# Revit family: BIG-1150-N
name_source: partatom
category: Plumbing Fixtures
units: mm (PartAtom-declared; Revit-internal decimal feet)

## family parameters
Always vertical = Yes
Cut with Voids When Loaded = Yes
OmniClass Number = 23.45.00.00
OmniClass Title = Sanitary, Laundry, and Cleaning Equipment
Part Type = Normal
Room Calculation Point = No
Round Connector Dimension = Use Diameter
Shared = No
Work Plane-Based = No

## types (1)
- BIG-1150-N
    Bottom Pipe RP = 8 13/32"
    Default Elevation = 0"
    Ext End = -20"
    Front Extude = 27 1/2"
    Height of Body = 50"
    Length = 83"
    Lid Height from Inlet/Outlet Center (15.5" Min. thru 24.5" Max.) = 24 1/4"
    Manufacturer = MIFAB
    Material = Polyethylene, High Density
    Model = BIG-1150-N
    Pipe RP = 38"
    Top RP 1 = 19"
    Top Vent = 9 7/16"
    URL = WWW,MIFAB.COM
    Vent = 40"
    Vent Pipe = 0"
    Vent height = 40"
    Vent/2 = 20"
    Vesibility-Vent = Yes
    Visibility-1 = No
    Visiblity = Yes
    Void 1 H = 6 1/16"
    Void 1 L = 14 9/32"
    Void 1 TL = 9 15/32"
    Width = 33 1/2"
    array = 2
    center void = 10"
    center void h = 4 1/4"
    pipe height = 12 1/2"
    v1 = No
    v2 = Yes

## geometry (parser evidence)
native form markers: Sweep x11
no freeform markers — native parametric forms only
